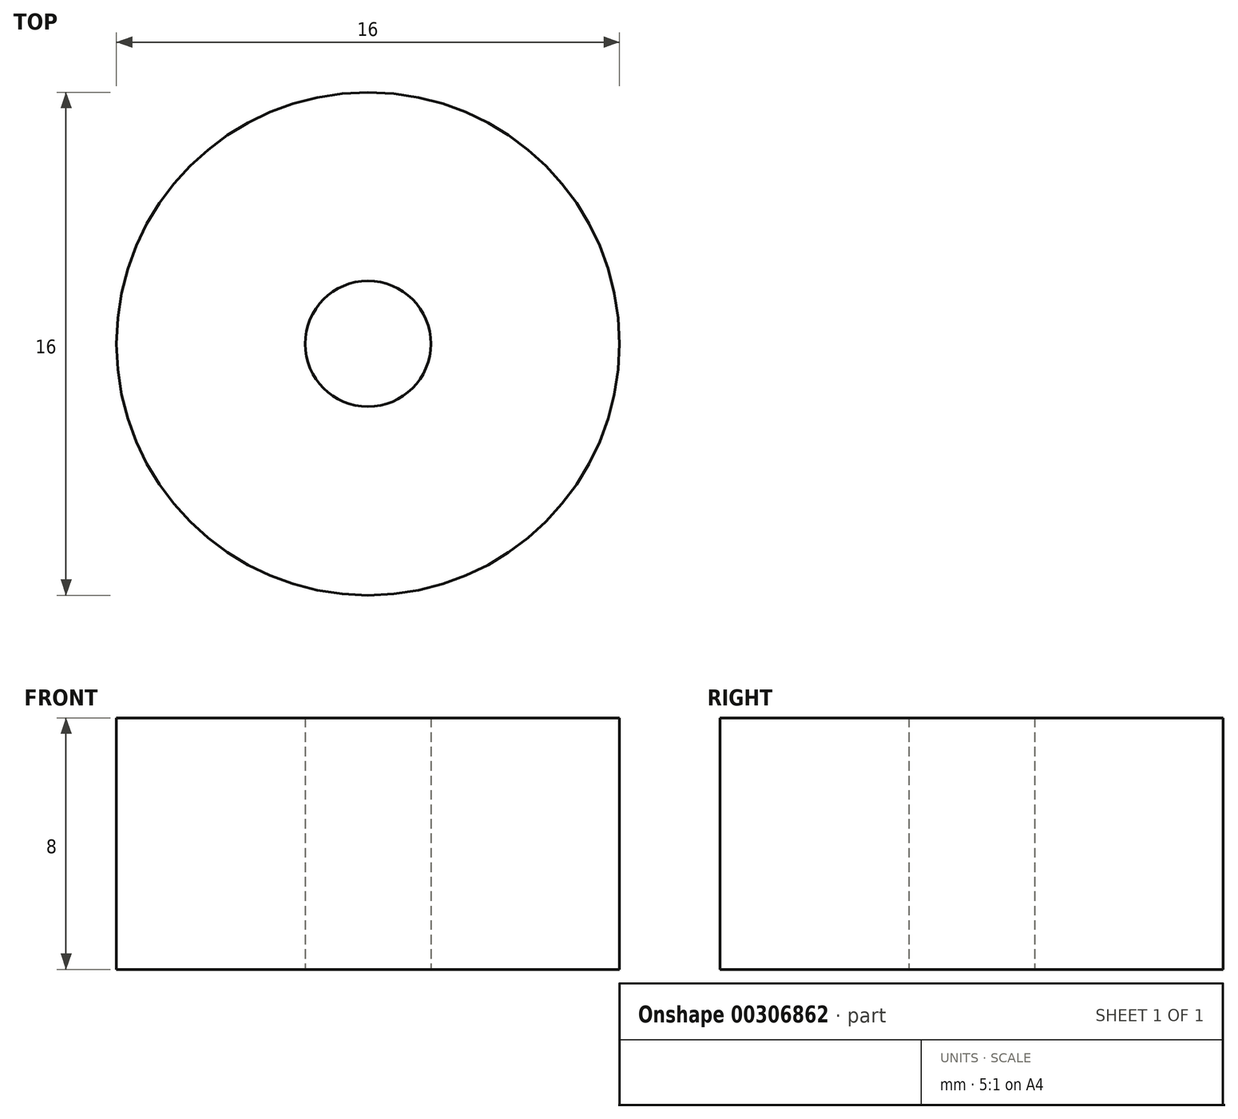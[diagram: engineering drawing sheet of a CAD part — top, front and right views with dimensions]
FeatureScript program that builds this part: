
annotation { "Feature Type Name" : "Feature", "Feature Type Description" : "" }
export const myFeature = defineFeature(function(context is Context, id is Id, definition is map)
    precondition{}
    {
        {
            var Q0;
            Q0=qCreatedBy(makeId("Top.planeOp"),FACE);
            var sketch = newSketch(context, id + "F0", { "sketchPlane" : qUnion([Q0])});
            skCircle(sketch, "E0", {"center": v(0, 0) * mm, "radius": 2 * mm});
            skCircle(sketch, "E1", {"center": v(0, 0) * mm, "radius": 8 * mm});
            skSolve(sketch);
        }
        {
            var Q0;
            Q0 = qSketchRegion(id + "F0", true);
            extrude(context, id + "F1", {"entities" : qUnion([Q0]), "depth" : 8 * mm, "offsetDistance" : 25 * mm});
        }
    });
